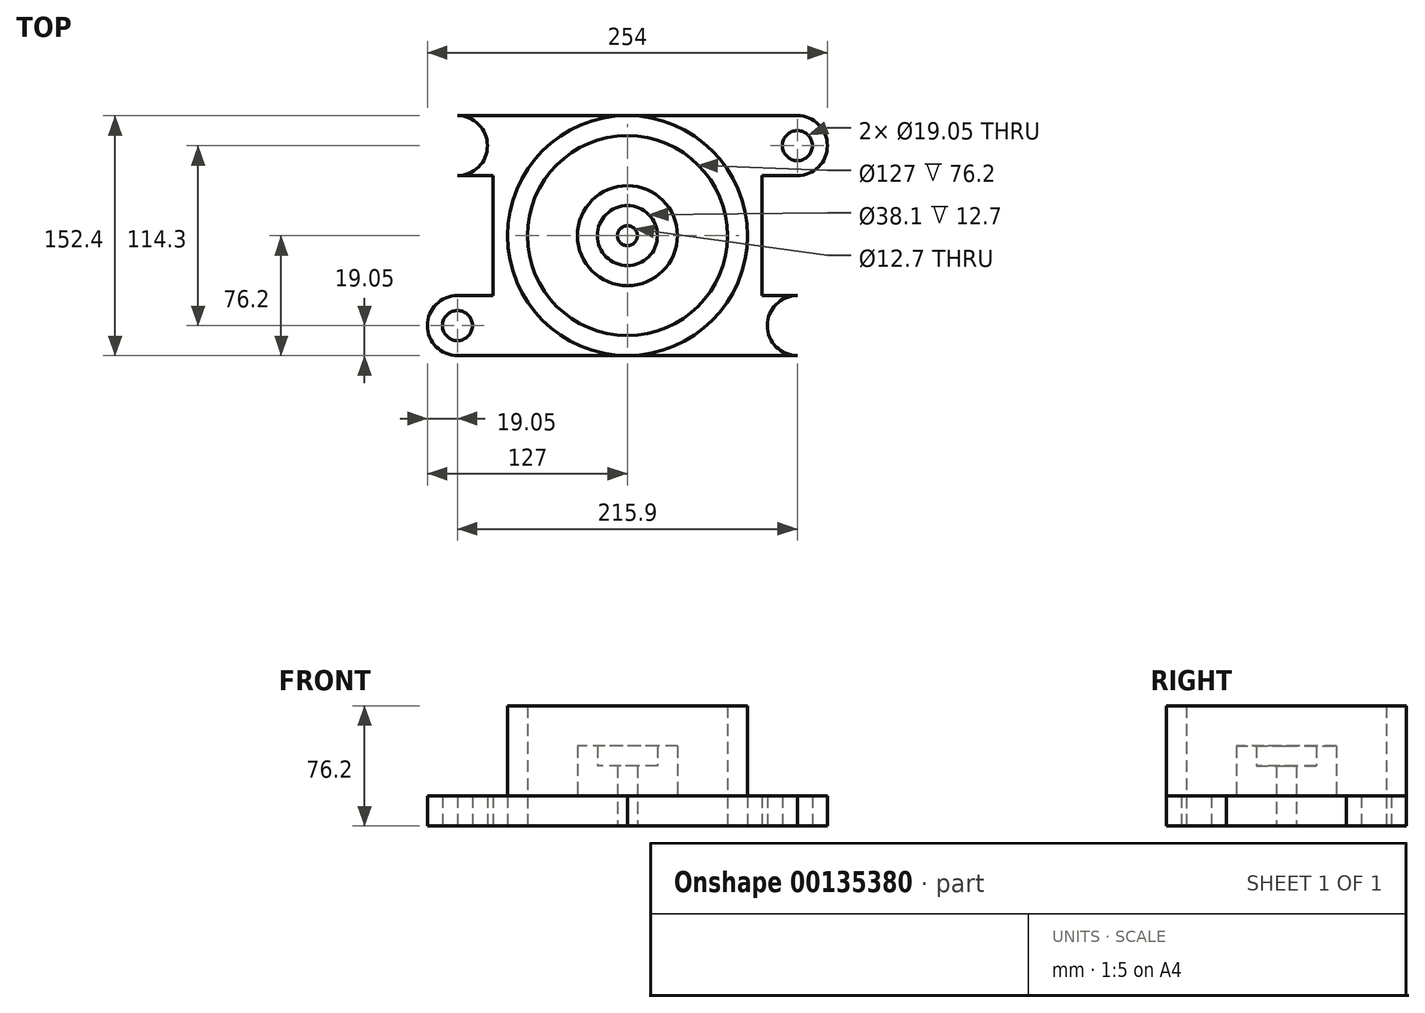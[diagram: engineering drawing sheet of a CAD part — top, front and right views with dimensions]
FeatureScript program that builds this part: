
annotation { "Feature Type Name" : "Feature", "Feature Type Description" : "" }
export const myFeature = defineFeature(function(context is Context, id is Id, definition is map)
    precondition{}
    {
        {
            var Q0;
            Q0=qCreatedBy(makeId("Top.planeOp"),FACE);
            var sketch = newSketch(context, id + "F0", { "sketchPlane" : qUnion([Q0])});
            skCircle(sketch, "E0", {"center": v(0, 0) * mm, "radius": 6.35 * mm});
            skCircle(sketch, "E1", {"center": v(0, 0) * mm, "radius": 19.05 * mm});
            skCircle(sketch, "E2", {"center": v(0, 0) * mm, "radius": 31.75 * mm});
            skCircle(sketch, "E3", {"center": v(0, 0) * mm, "radius": 63.5 * mm});
            skCircle(sketch, "E4", {"center": v(0, 0) * mm, "radius": 76.2 * mm});
            skLineSegment(sketch, "E5", {"start": v(0, -76.2) * mm, "end": v(-107.95, -76.2) * mm});
            skLineSegment(sketch, "E6", {"start": v(-107.95, -76.2) * mm, "end": v(-107.95, -38.1) * mm, "construction": true});
            skCircle(sketch, "E7", {"center": v(-107.95, -57.15) * mm, "radius": 19.05 * mm});
            skLineSegment(sketch, "E8", {"start": v(-107.95, -38.1) * mm, "end": v(-66, -38.1) * mm});
            skCircle(sketch, "E9.MirrorC", {"center": v(-107.95, 57.15) * mm, "radius": 19.05 * mm});
            skLineSegment(sketch, "E10.MirrorCS", {"start": v(-107.95, 38.1) * mm, "end": v(-66, 38.1) * mm});
            skLineSegment(sketch, "E11.MirrorCS", {"start": v(0, 76.2) * mm, "end": v(-107.95, 76.2) * mm});
            skLineSegment(sketch, "E12.MirrorCS", {"start": v(0, 76.2) * mm, "end": v(107.95, 76.2) * mm});
            skCircle(sketch, "E13.MirrorC", {"center": v(107.95, 57.15) * mm, "radius": 19.05 * mm});
            skLineSegment(sketch, "E14.MirrorCS", {"start": v(107.95, 38.1) * mm, "end": v(66, 38.1) * mm});
            skCircle(sketch, "E15.MirrorC", {"center": v(107.95, -57.15) * mm, "radius": 19.05 * mm});
            skLineSegment(sketch, "E16.MirrorCS", {"start": v(107.95, -38.1) * mm, "end": v(66, -38.1) * mm});
            skLineSegment(sketch, "E17.MirrorCS", {"start": v(0, -76.2) * mm, "end": v(107.95, -76.2) * mm});
            skLineSegment(sketch, "E18", {"start": v(-85.32, 38.1) * mm, "end": v(-85.32, -38.1) * mm});
            skLineSegment(sketch, "E19", {"start": v(85.32, 38.1) * mm, "end": v(85.32, -38.1) * mm});
            skCircle(sketch, "E20", {"center": v(-107.95, -57.15) * mm, "radius": 9.53 * mm});
            skCircle(sketch, "E21.MirrorC", {"center": v(-107.95, 57.15) * mm, "radius": 9.53 * mm});
            skCircle(sketch, "E22.MirrorC", {"center": v(107.95, 57.15) * mm, "radius": 9.53 * mm});
            skCircle(sketch, "E23.MirrorC", {"center": v(107.95, -57.15) * mm, "radius": 9.53 * mm});
            skSolve(sketch);
        }
        {
            var Q0;
            {var subQ4=sQuery(id+"F0.wireOp",EDGE,"E5");Q0=makeQuery(id+"F0.imprint","IMPRINT",FACE,{"disambiguationData":[TD([[makeQuery(id+"F0.imprint","IMPRINT",EDGE,{"derivedFrom":subQ4}),-1.0]])]});}
            var Q1;
            {var subQ4=sQuery(id+"F0.wireOp",EDGE,"E11.MirrorCS");Q1=makeQuery(id+"F0.imprint","IMPRINT",FACE,{"disambiguationData":[TD([[makeQuery(id+"F0.imprint","IMPRINT",EDGE,{"derivedFrom":subQ4}),1.0]])]});}
            var Q2;
            {var subQ0=sQuery(id+"F0.wireOp",EDGE,"E9.MirrorC");var subQ1=makeQuery(id+"F0.imprint","INTERSECT",VERTEX,{"derivedFrom":[subQ0,sQuery(id+"F0.wireOp",EDGE,"E10.MirrorCS")]});Q2=makeQuery(id+"F0.imprint","IMPRINT",FACE,{"disambiguationData":[TD([[makeQuery(id+"F0.imprint","IMPRINT",EDGE,{"disambiguationData":[TD([[subQ1,-1.0]])],"derivedFrom":subQ0}),-1.0]])]});}
            var Q3;
            {var subQ0=sQuery(id+"F0.wireOp",EDGE,"E7");var subQ1=makeQuery(id+"F0.imprint","INTERSECT",VERTEX,{"derivedFrom":[sQuery(id+"F0.wireOp",EDGE,"E5"),subQ0]});Q3=makeQuery(id+"F0.imprint","IMPRINT",FACE,{"disambiguationData":[TD([[makeQuery(id+"F0.imprint","IMPRINT",EDGE,{"disambiguationData":[TD([[subQ1,1.0]])],"derivedFrom":subQ0}),1.0]])]});}
            var Q4;
            {var subQ4=sQuery(id+"F0.wireOp",EDGE,"E12.MirrorCS");Q4=makeQuery(id+"F0.imprint","IMPRINT",FACE,{"disambiguationData":[TD([[makeQuery(id+"F0.imprint","IMPRINT",EDGE,{"derivedFrom":subQ4}),-1.0]])]});}
            var Q5;
            {var subQ0=sQuery(id+"F0.wireOp",EDGE,"E13.MirrorC");var subQ1=makeQuery(id+"F0.imprint","INTERSECT",VERTEX,{"derivedFrom":[sQuery(id+"F0.wireOp",EDGE,"E12.MirrorCS"),subQ0]});Q5=makeQuery(id+"F0.imprint","IMPRINT",FACE,{"disambiguationData":[TD([[makeQuery(id+"F0.imprint","IMPRINT",EDGE,{"disambiguationData":[TD([[subQ1,1.0]])],"derivedFrom":subQ0}),1.0]])]});}
            var Q6;
            {var subQ4=sQuery(id+"F0.wireOp",EDGE,"E17.MirrorCS");Q6=makeQuery(id+"F0.imprint","IMPRINT",FACE,{"disambiguationData":[TD([[makeQuery(id+"F0.imprint","IMPRINT",EDGE,{"derivedFrom":subQ4}),1.0]])]});}
            var Q7;
            {var subQ0=sQuery(id+"F0.wireOp",EDGE,"E15.MirrorC");var subQ1=makeQuery(id+"F0.imprint","INTERSECT",VERTEX,{"derivedFrom":[subQ0,sQuery(id+"F0.wireOp",EDGE,"E16.MirrorCS")]});Q7=makeQuery(id+"F0.imprint","IMPRINT",FACE,{"disambiguationData":[TD([[makeQuery(id+"F0.imprint","IMPRINT",EDGE,{"disambiguationData":[TD([[subQ1,-1.0]])],"derivedFrom":subQ0}),-1.0]])]});}
            var Q8;
            Q8=makeQuery(id+"F0.imprint","IMPRINT",FACE,{"disambiguationData":[TD([[makeQuery(id+"F0.imprint","IMPRINT",EDGE,{"derivedFrom":sQuery(id+"F0.wireOp",EDGE,"E2")}),-1.0]])]});
            var Q9;
            {var subQ5=sQuery(id+"F0.wireOp",EDGE,"E18");Q9=makeQuery(id+"F0.imprint","IMPRINT",FACE,{"disambiguationData":[TD([[makeQuery(id+"F0.imprint","IMPRINT",EDGE,{"derivedFrom":subQ5}),1.0]])]});}
            var Q10;
            {var subQ0=sQuery(id+"F0.wireOp",EDGE,"E14.MirrorCS");var subQ1=sQuery(id+"F0.wireOp",EDGE,"E4");var subQ2=makeQuery(id+"F0.imprint","INTERSECT",VERTEX,{"derivedFrom":[subQ1,subQ0]});Q10=makeQuery(id+"F0.imprint","IMPRINT",FACE,{"disambiguationData":[TD([[makeQuery(id+"F0.imprint","IMPRINT",EDGE,{"disambiguationData":[TD([[subQ2,1.0]])],"derivedFrom":subQ1}),-1.0]])]});}
            var Q11;
            {var subQ0=sQuery(id+"F0.wireOp",EDGE,"E16.MirrorCS");var subQ1=sQuery(id+"F0.wireOp",EDGE,"E4");var subQ2=makeQuery(id+"F0.imprint","INTERSECT",VERTEX,{"derivedFrom":[subQ1,subQ0]});Q11=makeQuery(id+"F0.imprint","IMPRINT",FACE,{"disambiguationData":[TD([[makeQuery(id+"F0.imprint","IMPRINT",EDGE,{"disambiguationData":[TD([[subQ2,-1.0]])],"derivedFrom":subQ1}),-1.0]])]});}
            extrude(context, id + "F1", {"entities" : qUnion([Q0, Q1, Q2, Q3, Q4, Q5, Q6, Q7, Q8, Q9, Q10, Q11]), "depth" : 19.05 * mm});
        }
        {
            var Q0;
            Q0=makeQuery(id+"F0.imprint","IMPRINT",FACE,{"disambiguationData":[TD([[makeQuery(id+"F0.imprint","IMPRINT",EDGE,{"derivedFrom":sQuery(id+"F0.wireOp",EDGE,"E3")}),-1.0]])]});
            extrude(context, id + "F2", {"entities" : qUnion([Q0]), "depth" : 76.2 * mm});
        }
        {
            var Q0;
            Q0=makeQuery(id+"F0.imprint","IMPRINT",FACE,{"disambiguationData":[TD([[makeQuery(id+"F0.imprint","IMPRINT",EDGE,{"derivedFrom":sQuery(id+"F0.wireOp",EDGE,"E1")}),-1.0]])]});
            extrude(context, id + "F3", {"entities" : qUnion([Q0]), "operationType" : NewBodyOperationType.ADD, "depth" : 50.8 * mm});
        }
        {
            var Q0;
            Q0=makeQuery(id+"F0.imprint","IMPRINT",FACE,{"disambiguationData":[TD([[makeQuery(id+"F0.imprint","IMPRINT",EDGE,{"derivedFrom":sQuery(id+"F0.wireOp",EDGE,"E0")}),-1.0]])]});
            extrude(context, id + "F4", {"entities" : qUnion([Q0]), "operationType" : NewBodyOperationType.ADD, "depth" : 38.1 * mm});
        }
    });
